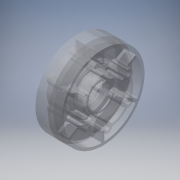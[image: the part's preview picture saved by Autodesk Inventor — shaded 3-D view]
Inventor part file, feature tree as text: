
AUTODESK INVENTOR PART (.ipt)
format: ipt  version: 2016 (Build 200138000, 138)  size: 1,613,312 bytes
history: native  units: in
note: dims shown in document units (in); Inventor stores cm internally (conversion verified against a paired STEP export)
features: fillet x2
ambient origin geometry x8: Origin, YZ Plane, XZ Plane, XY Plane, X Axis, Y Axis, Z Axis, Center Point
bodies: Solid1 (feature_tree), Solid2 (feature_tree)
feature tree (2):
  fillet  "Fillet10"  [1 undecoded]
  fillet  "Fillet9"  [1 undecoded]
note: 2 required parameter values undecoded (feature->parameter linkage not recoverable at this tier; creation-order binding heuristic only, values carry confidence <= 0.55)
